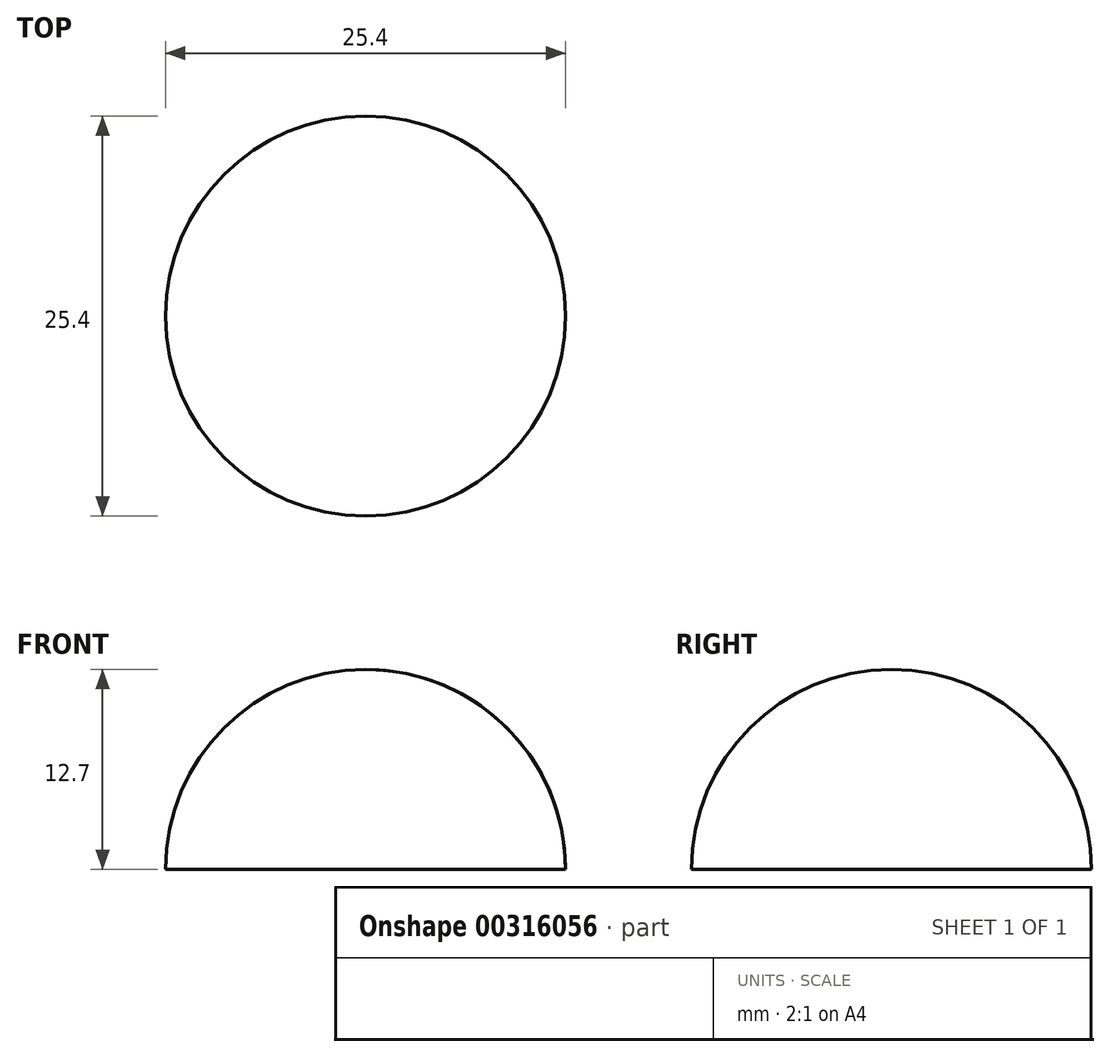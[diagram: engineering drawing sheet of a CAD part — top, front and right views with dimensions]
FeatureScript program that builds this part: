
annotation { "Feature Type Name" : "Feature", "Feature Type Description" : "" }
export const myFeature = defineFeature(function(context is Context, id is Id, definition is map)
    precondition{}
    {
        {
            var Q0;
            Q0=qCreatedBy(makeId("Front.planeOp"),FACE);
            var sketch = newSketch(context, id + "F0", { "sketchPlane" : qUnion([Q0])});
            skLineSegment(sketch, "E0", {"start": v(0, 0) * mm, "end": v(12.7, 0) * mm});
            skArc(sketch, "E1", {"start": v(12.7, 0) * mm, "mid": v(8.98, 8.98) * mm, "end": v(0, 12.7) * mm});
            skLineSegment(sketch, "E2", {"start": v(0, 0) * mm, "end": v(0, 12.7) * mm});
            skSolve(sketch);
        }
        {
            var Q0;
            Q0=qCreatedBy(makeId("Front.planeOp"),FACE);
            var sketch = newSketch(context, id + "F1", { "sketchPlane" : qUnion([Q0])});
            skLineSegment(sketch, "E3", {"start": v(0, 0) * mm, "end": v(0, 53.26) * mm, "construction": true});
            skSolve(sketch);
        }
        {
            var Q0;
            Q0 = qSketchRegion(id + "F0", true);
            var Q1;
            Q1=sQuery(id+"F1.wireOp",EDGE,"E3");
            revolve(context, id + "F2", {"entities" : qUnion([Q0]), "axis" : qUnion([Q1]), "revolveType" : RevolveType.FULL, "surfaceOperationType" : NewSurfaceOperationType.NEW});
        }
    });
